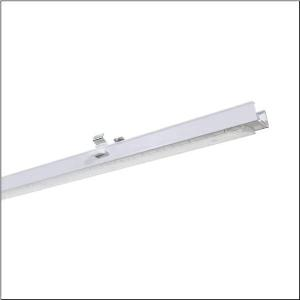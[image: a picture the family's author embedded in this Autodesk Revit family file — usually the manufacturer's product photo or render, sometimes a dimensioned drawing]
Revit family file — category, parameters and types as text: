
# Revit family: trunking_flex_31_51re11mb4cb
name_source: partatom
category: Lighting Fixtures
units: mm (PartAtom-declared; Revit-internal decimal feet)

## family parameters
Cut with Voids When Loaded = No
Host = Face
Light Source = No
Part Type = Normal
Room Calculation Point = No
Round Connector Dimension = Use Diameter
Shared = No

## types (1)
- --- (1 x LED, 11500 lm, 66 W, 4000K)
    Apparent Load = 66 VA
    CIE Flux Codes = 83 93 98 100 100
    Color Rendering = 80
    Color Temperature = 4000K
    Default Elevation = 1800 mm
    Description = Trunking Flex 31, luminaire insert, of extruded aluminium section, coated, traffic white (RAL 9016), length: 1.472mm, width: 91mm, height: 53mm, LED rated luminous flux: 11.500lm, light colour: 840, control gear: ON/OFF Multilumen, with system connector: socket, mains connection: 220..240V, AC, 50/60Hz, rated input power: 66W, luminous flux adjustable on luminaire in eight steps (3450/4380/5800/6700/8350/9200/10500/11500lm ), connected load according to luminous flux setting (19/24/32/37/47/52/60/66W), primary light control with lens, of plastic, primary optical cover: cover, of PMMA, light emission: direct distribution, protection rating (complete): IP20, insulation class (complete): insulation class I (protective earthing), certification: CE, UKCA, impact resistance: IK02, permissible ambient temperature for indoor applications: -20..+40°C, packaging unit: 1 piece
    Height = 58 mm
    Lamp = 1 x LED
    Lamp Light Flux = 11500 lm
    Lamp Power = 66 W
    Lamp count = 1
    Length = 1472 mm
    Luminous efficacy = 174 lm/W
    Manufacturer = Siteco
    ModVariant = No
    Model = 51RE11MB4CB
    Mounting Place = Ceiling
    Mounting Type = Pendant
    Number of Poles = 1
    OnlyDefault = Yes
    Power Factor = 1
    Product Name = Trunking Flex 31
    Product group = luminaire insert
    ProductGroupID = 901
    Protection Class = Protection class I
    Protection Degree = IP 20
    RLX_Detail_Level = 1
    RLX_Emergency_Light_Flux = 0 lm
    RLX_Emergency_Type = 0
    RLX_Emergency_Type_DB = No
    RlxData = <blob elided: 20953 chars, md5=49be886e>
    Socket = socket
    Standby Power = 0 W
    System Light Flux = 11500 lm
    System Power = 66 W
    Type Comments = factory setting: luminous flux: 100 % | (ON | ON | ON)
    Type Image = l_1266702.jpg
    URL = http://relux.com
    VarID = @adj_018775
    Voltage = 0 V
    Weight = 0.00 kg
    Width = 65 mm

## geometry (parser evidence)
native form markers: Blend x4, Sweep x10
no freeform markers — native parametric forms only
